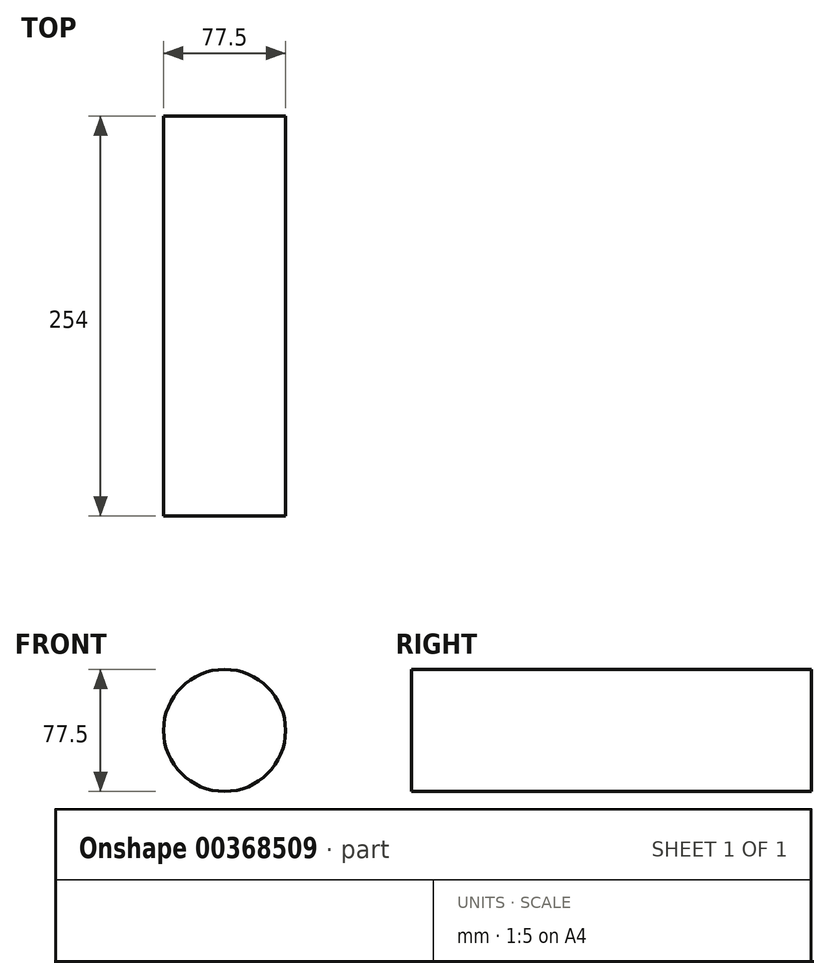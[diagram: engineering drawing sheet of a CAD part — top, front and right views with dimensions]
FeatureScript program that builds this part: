
annotation { "Feature Type Name" : "Feature", "Feature Type Description" : "" }
export const myFeature = defineFeature(function(context is Context, id is Id, definition is map)
    precondition{}
    {
        {
            var Q0;
            Q0=qCreatedBy(makeId("Front.planeOp"),FACE);
            var sketch = newSketch(context, id + "F0", { "sketchPlane" : qUnion([Q0])});
            skCircle(sketch, "E0", {"center": v(0, 0) * mm, "radius": 38.75 * mm});
            skSolve(sketch);
        }
        {
            var Q0;
            Q0=makeQuery(id+"F0.imprint","IMPRINT",FACE,{"disambiguationData":[TD([[makeQuery(id+"F0.imprint","IMPRINT",EDGE,{"derivedFrom":sQuery(id+"F0.wireOp",EDGE,"E0")}),1.0]])]});
            extrude(context, id + "F1", {"entities" : qUnion([Q0]), "depth" : 254 * mm});
        }
    });
